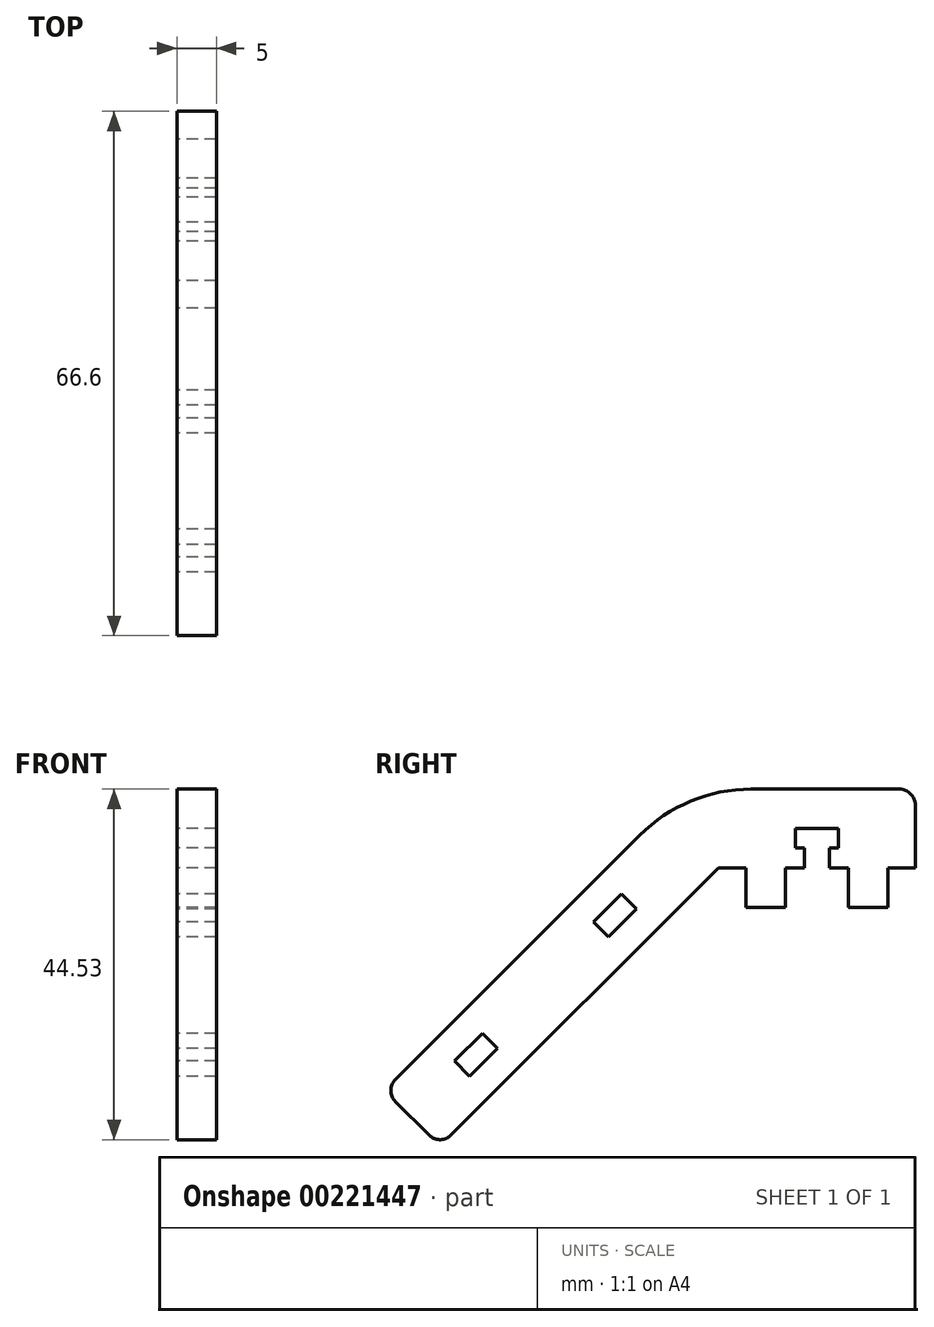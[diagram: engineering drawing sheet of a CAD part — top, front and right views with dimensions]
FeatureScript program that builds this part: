
annotation { "Feature Type Name" : "Feature", "Feature Type Description" : "" }
export const myFeature = defineFeature(function(context is Context, id is Id, definition is map)
    precondition{}
    {
        {
            assignVariable(context, id + "F0", {"name" : "thickness", "anyValue" : 5 * mm});
        }
        {
            var Q0;
            Q0=qCreatedBy(makeId("Right.planeOp"),FACE);
            var sketch = newSketch(context, id + "F1", { "sketchPlane" : qUnion([Q0])});
            skLineSegment(sketch, "E0", {"start": v(0, 0) * mm, "end": v(-10.9, 0) * mm});
            skLineSegment(sketch, "E1", {"start": v(-25, 0) * mm, "end": v(-58.94, -33.94) * mm});
            skLineSegment(sketch, "E2", {"start": v(0, 0) * mm, "end": v(0, 8) * mm});
            skLineSegment(sketch, "E3", {"start": v(-2, 10) * mm, "end": v(-20.86, 10) * mm});
            skLineSegment(sketch, "E4", {"start": v(-35, 4.14) * mm, "end": v(-66.01, -26.87) * mm});
            skLineSegment(sketch, "E5", {"start": v(-66.01, -29.7) * mm, "end": v(-61.77, -33.94) * mm});
            skLineSegment(sketch, "E6", {"start": v(-3.5, 0) * mm, "end": v(-3.5, -5) * mm});
            skLineSegment(sketch, "E7", {"start": v(-3.5, -5) * mm, "end": v(-8.5, -5) * mm});
            skLineSegment(sketch, "E8", {"start": v(-8.5, -5) * mm, "end": v(-8.5, 0) * mm});
            skLineSegment(sketch, "E9", {"start": v(-16.5, 0) * mm, "end": v(-16.5, -5) * mm});
            skLineSegment(sketch, "E10", {"start": v(-16.5, -5) * mm, "end": v(-21.5, -5) * mm});
            skLineSegment(sketch, "E11", {"start": v(-21.5, -5) * mm, "end": v(-21.5, 0) * mm});
            skLineSegment(sketch, "E12", {"start": v(-12.5, 0) * mm, "end": v(-12.5, 10) * mm, "construction": true});
            skLineSegment(sketch, "E13", {"start": v(-14.1, 0) * mm, "end": v(-14.1, 2.5) * mm});
            skLineSegment(sketch, "E14", {"start": v(-14.1, 2.5) * mm, "end": v(-15.25, 2.5) * mm});
            skLineSegment(sketch, "E15", {"start": v(-15.25, 2.5) * mm, "end": v(-15.25, 5) * mm});
            skLineSegment(sketch, "E16", {"start": v(-15.25, 5) * mm, "end": v(-12.5, 5) * mm});
            skLineSegment(sketch, "E17.MirrorCS", {"start": v(-9.75, 5) * mm, "end": v(-12.5, 5) * mm});
            skLineSegment(sketch, "E18.MirrorCS", {"start": v(-9.75, 2.5) * mm, "end": v(-9.75, 5) * mm});
            skLineSegment(sketch, "E19.MirrorCS", {"start": v(-10.9, 2.5) * mm, "end": v(-9.75, 2.5) * mm});
            skLineSegment(sketch, "E20.MirrorCS", {"start": v(-10.9, 0) * mm, "end": v(-10.9, 2.5) * mm});
            skLineSegment(sketch, "E21.trimOffspring", {"start": v(-14.1, 0) * mm, "end": v(-25, 0) * mm});
            skPoint(sketch, "E22.visualSharp", {"position": v(-29.14, 10) * mm});
            skArc(sketch, "E22.filletArc", {"start": v(-20.86, 10) * mm, "mid": v(-28.51, 8.48) * mm, "end": v(-35, 4.14) * mm});
            skPoint(sketch, "E23.visualSharp", {"position": v(-67.43, -28.28) * mm});
            skArc(sketch, "E23.filletArc", {"start": v(-66.01, -26.87) * mm, "mid": v(-66.6, -28.28) * mm, "end": v(-66.01, -29.7) * mm});
            skPoint(sketch, "E24.visualSharp", {"position": v(-60.36, -35.36) * mm});
            skArc(sketch, "E24.filletArc", {"start": v(-61.77, -33.94) * mm, "mid": v(-60.36, -34.53) * mm, "end": v(-58.94, -33.94) * mm});
            skPoint(sketch, "E25.visualSharp", {"position": v(0, 10) * mm});
            skArc(sketch, "E25.filletArc", {"start": v(0, 8) * mm, "mid": v(-0.59, 9.41) * mm, "end": v(-2, 10) * mm});
            skLineSegment(sketch, "E26", {"start": v(-37.32, -3.34) * mm, "end": v(-40.85, -6.87) * mm});
            skLineSegment(sketch, "E27", {"start": v(-40.85, -6.87) * mm, "end": v(-38.94, -8.78) * mm});
            skLineSegment(sketch, "E28", {"start": v(-38.94, -8.78) * mm, "end": v(-35.4, -5.25) * mm});
            skLineSegment(sketch, "E29", {"start": v(-35.4, -5.25) * mm, "end": v(-37.32, -3.34) * mm});
            skLineSegment(sketch, "E30", {"start": v(-50.5, -11.36) * mm, "end": v(-43.44, -18.44) * mm, "construction": true});
            skLineSegment(sketch, "E31", {"start": v(-39.14, 0) * mm, "end": v(-32.07, -7.07) * mm, "construction": true});
            skLineSegment(sketch, "E32.MirrorCS", {"start": v(-58.53, -24.55) * mm, "end": v(-55, -21.02) * mm});
            skLineSegment(sketch, "E33.MirrorCS", {"start": v(-55, -21.02) * mm, "end": v(-53.09, -22.93) * mm});
            skLineSegment(sketch, "E34.MirrorCS", {"start": v(-53.09, -22.93) * mm, "end": v(-56.62, -26.46) * mm});
            skLineSegment(sketch, "E35.MirrorCS", {"start": v(-56.62, -26.46) * mm, "end": v(-58.53, -24.55) * mm});
            skLineSegment(sketch, "E36", {"start": v(-63.9, -31.82) * mm, "end": v(-35.6, -3.54) * mm, "construction": true});
            skPoint(sketch, "E37", {"position": v(-57.58, -25.5) * mm});
            skSolve(sketch);
        }
        {
            var Q0;
            Q0 = qSketchRegion(id + "F1", true);
            extrude(context, id + "F2", {"entities" : qUnion([Q0]), "depth" : getVariable(context, 'thickness')});
        }
    });
